# Revit family: TUB
name_source: partatom
category: Mechanical Equipment
units: mm (PartAtom-declared; Revit-internal decimal feet)

## family parameters
Always vertical = Yes
Cut with Voids When Loaded = No
Part Type = Normal
Room Calculation Point = No
Round Connector Dimension = Use Diameter
Shared = No
Work Plane-Based = No

## types (18) — shared parameters
0 = 0' - 0"
1" = 0' - 1"
1' = 1' - 0"
1.5 = 0' - 1 1/2"
2" = 0' - 2"
2' = 2' - 0"
4" = 0' - 4"
D = 0' - 4"
Manufacturer = Loren Cook Company
ONE EIGTH = 0' - 0 1/8"
URL = www.lorencook.com

## per-type parameters (varying)
| type | (A/2)-4" | (A/2)-4.125" | (T_SQ/2)+.125" | -(A/2) | -(C/2) | A | A/2 | A/4 | B | B/2 | C-B | C-B-3" | C_ | C_/2 | E | E+C-B-2" | E-.125" | Model | RO | T_SQ | T_SQ/2 | T_SQ/6 | Type Comments |
| 24_TUB | 0' - 11 5/8" | 0' - 11 1/2" | 1' - 6 1/8" | -1' - 3 5/8" | -0' - 9 9/16" | 2' - 7 1/4" | 1' - 3 5/8" | 0' - 10 13/32" | 1' - 7 1/8" | 0' - 9 9/16" | 2' - 5 1/4" | 2' - 2 1/4" | 4' - 0 3/8" | 2' - 0 3/16" | 0' - 3" | 2' - 6 1/4" | 0' - 2 7/8" | TUB | 2' - 7 1/2" | 3' - 0" | 1' - 6" | 0' - 6" | Upblast Exhaust Ventilator Triton Steel Propeller Roof Mounted/ Belt Drive |
| 30_TUB_SC | 1' - 2 5/8" | 1' - 2 1/2" | 1' - 9 1/8" | -1' - 6 5/8" | -0' - 11 13/16" | 3' - 1 1/4" | 1' - 6 5/8" | 1' - 0 13/32" | 1' - 11 5/8" | 0' - 11 13/16" | 2' - 6 1/2" | 2' - 3 1/2" | 4' - 6 1/8" | 2' - 3 1/16" | 0' - 3" | 2' - 7 1/2" | 0' - 2 7/8" | TUBSC | 3' - 1 1/2" | 3' - 6" | 1' - 9" | 0' - 7" | Upblast Exhaust Smoke Control Ventilator Triton Steel Propeller Roof Mounted/ Belt Drive |
| 36_TUB_SC | 1' - 5 5/8" | 1' - 5 1/2" | 2' - 0 1/8" | -1' - 9 5/8" | -1' - 0 13/16" | 3' - 7 1/4" | 1' - 9 5/8" | 1' - 2 13/32" | 2' - 1 5/8" | 1' - 0 13/16" | 2' - 11 1/2" | 2' - 8 1/2" | 5' - 1 1/8" | 2' - 6 9/16" | 0' - 3" | 3' - 0 1/2" | 0' - 2 7/8" | TUBSC | 3' - 7 1/2" | 4' - 0" | 2' - 0" | 0' - 8" | Upblast Exhaust Smoke Control Ventilator Triton Steel Propeller Roof Mounted/ Belt Drive |
| 42_TUB_SC | 1' - 8 5/8" | 1' - 8 1/2" | 2' - 3 1/8" | -2' - 0 5/8" | -1' - 1 15/16" | 4' - 1 1/4" | 2' - 0 5/8" | 1' - 4 13/32" | 2' - 3 7/8" | 1' - 1 15/16" | 3' - 0 11/16" | 2' - 9 11/16" | 5' - 4 9/16" | 2' - 8 9/32" | 0' - 3" | 3' - 1 11/16" | 0' - 2 7/8" | TUBSC | 4' - 1 1/2" | 4' - 6" | 2' - 3" | 0' - 9" | Upblast Exhaust Smoke Control Ventilator Triton Steel Propeller Roof Mounted/ Belt Drive |
| 48_TUB | 1' - 11 5/8" | 1' - 11 1/2" | 2' - 6 1/8" | -2' - 3 5/8" | -1' - 3 5/8" | 4' - 7 1/4" | 2' - 3 5/8" | 1' - 6 13/32" | 2' - 7 1/4" | 1' - 3 5/8" | 3' - 3 9/16" | 3' - 0 9/16" | 5' - 10 13/16" | 2' - 11 13/32" | 0' - 3" | 3' - 4 9/16" | 0' - 2 7/8" | TUB | 4' - 7 1/2" | 5' - 0" | 2' - 6" | 0' - 10" | Upblast Exhaust Ventilator Triton Steel Propeller Roof Mounted/ Belt Drive |
| 54_TUB | 2' - 2 5/8" | 2' - 2 1/2" | 2' - 9 1/8" | -2' - 6 5/8" | -1' - 5 5/8" | 5' - 1 1/4" | 2' - 6 5/8" | 1' - 8 13/32" | 2' - 11 1/4" | 1' - 5 5/8" | 3' - 8" | 3' - 5" | 6' - 7 1/4" | 3' - 3 5/8" | 0' - 3" | 3' - 9" | 0' - 2 7/8" | TUB | 5' - 1 1/2" | 5' - 6" | 2' - 9" | 0' - 11" | Upblast Exhaust Ventilator Triton Steel Propeller Roof Mounted/ Belt Drive |
| 60_TUB | 2' - 5 5/8" | 2' - 5 1/2" | 3' - 0 1/8" | -2' - 9 5/8" | -1' - 6 1/4" | 5' - 7 1/4" | 2' - 9 5/8" | 1' - 10 13/32" | 3' - 0 1/2" | 1' - 6 1/4" | 3' - 11 1/4" | 3' - 8 1/4" | 6' - 11 3/4" | 3' - 5 7/8" | 0' - 3" | 4' - 0 1/4" | 0' - 2 7/8" | TUB | 5' - 7 1/2" | 6' - 0" | 3' - 0" | 1' - 0" | Upblast Exhaust Ventilator Triton Steel Propeller Roof Mounted/ Belt Drive |
| 72_TUB | 2' - 11 1/2" | 2' - 11 3/8" | 3' - 6 1/8" | -3' - 3 1/2" | -1' - 10" | 6' - 7" | 3' - 3 1/2" | 2' - 2 11/32" | 3' - 8" | 1' - 10" | 4' - 6 13/16" | 4' - 3 13/16" | 8' - 2 13/16" | 4' - 1 13/32" | 0' - 3" | 4' - 7 13/16" | 0' - 2 7/8" | TUB | 6' - 7 1/2" | 7' - 0" | 3' - 6" | 1' - 2" | Upblast Exhaust Ventilator Triton Steel Propeller Roof Mounted/ Belt Drive |
| 20_TUB | 0' - 9 5/8" | 0' - 9 1/2" | 1' - 4 1/8" | -1' - 1 5/8" | -0' - 9 1/16" | 2' - 3 1/4" | 1' - 1 5/8" | 0' - 9 3/32" | 1' - 6 1/8" | 0' - 9 1/16" | 2' - 5 5/8" | 2' - 2 5/8" | 3' - 11 3/4" | 1' - 11 7/8" | 0' - 2" | 2' - 5 5/8" | 0' - 1 7/8" | TUB | 2' - 3 1/2" | 2' - 8" | 1' - 4" | 0' - 5 11/32" | Upblast Exhaust Ventilator Triton Steel Propeller Roof Mounted/ Belt Drive |
| 20_TUB_SC | 0' - 9 5/8" | 0' - 9 1/2" | 1' - 4 1/8" | -1' - 1 5/8" | -0' - 9 1/16" | 2' - 3 1/4" | 1' - 1 5/8" | 0' - 9 3/32" | 1' - 6 1/8" | 0' - 9 1/16" | 2' - 5 5/8" | 2' - 2 5/8" | 3' - 11 3/4" | 1' - 11 7/8" | 0' - 2" | 2' - 5 5/8" | 0' - 1 7/8" | TUBSC | 2' - 3 1/2" | 2' - 8" | 1' - 4" | 0' - 5 11/32" | Upblast Exhaust Smoke Control Ventilator Triton Steel Propeller Roof Mounted/ Belt Drive |
| 24_TUB_SC | 0' - 11 5/8" | 0' - 11 1/2" | 1' - 6 1/8" | -1' - 3 5/8" | -0' - 9 9/16" | 2' - 7 1/4" | 1' - 3 5/8" | 0' - 10 13/32" | 1' - 7 1/8" | 0' - 9 9/16" | 2' - 5 1/4" | 2' - 2 1/4" | 4' - 0 3/8" | 2' - 0 3/16" | 0' - 3" | 2' - 6 1/4" | 0' - 2 7/8" | TUBSC | 2' - 7 1/2" | 3' - 0" | 1' - 6" | 0' - 6" | Upblast Exhaust Smoke Control Ventilator Triton Steel Propeller Roof Mounted/ Belt Drive |
| 48_TUB_SC | 1' - 11 5/8" | 1' - 11 1/2" | 2' - 6 1/8" | -2' - 3 5/8" | -1' - 3 5/8" | 4' - 7 1/4" | 2' - 3 5/8" | 1' - 6 13/32" | 2' - 7 1/4" | 1' - 3 5/8" | 3' - 3 9/16" | 3' - 0 9/16" | 5' - 10 13/16" | 2' - 11 13/32" | 0' - 3" | 3' - 4 9/16" | 0' - 2 7/8" | TUBSC | 4' - 7 1/2" | 5' - 0" | 2' - 6" | 0' - 10" | Upblast Exhaust Smoke Control Ventilator Triton Steel Propeller Roof Mounted/ Belt Drive |
| 30_TUB | 1' - 2 5/8" | 1' - 2 1/2" | 1' - 9 1/8" | -1' - 6 5/8" | -0' - 11 13/16" | 3' - 1 1/4" | 1' - 6 5/8" | 1' - 0 13/32" | 1' - 11 5/8" | 0' - 11 13/16" | 2' - 6 1/2" | 2' - 3 1/2" | 4' - 6 1/8" | 2' - 3 1/16" | 0' - 3" | 2' - 7 1/2" | 0' - 2 7/8" | TUB | 3' - 1 1/2" | 3' - 6" | 1' - 9" | 0' - 7" | Upblast Exhaust Ventilator Triton Steel Propeller Roof Mounted/ Belt Drive |
| 36_TUB | 1' - 5 5/8" | 1' - 5 1/2" | 2' - 0 1/8" | -1' - 9 5/8" | -1' - 0 13/16" | 3' - 7 1/4" | 1' - 9 5/8" | 1' - 2 13/32" | 2' - 1 5/8" | 1' - 0 13/16" | 2' - 11 1/2" | 2' - 8 1/2" | 5' - 1 1/8" | 2' - 6 9/16" | 0' - 3" | 3' - 0 1/2" | 0' - 2 7/8" | TUB | 3' - 7 1/2" | 4' - 0" | 2' - 0" | 0' - 8" | Upblast Exhaust Ventilator Triton Steel Propeller Roof Mounted/ Belt Drive |
| 42_TUB | 1' - 8 5/8" | 1' - 8 1/2" | 2' - 3 1/8" | -2' - 0 5/8" | -1' - 1 15/16" | 4' - 1 1/4" | 2' - 0 5/8" | 1' - 4 13/32" | 2' - 3 7/8" | 1' - 1 15/16" | 3' - 0 11/16" | 2' - 9 11/16" | 5' - 4 9/16" | 2' - 8 9/32" | 0' - 3" | 3' - 1 11/16" | 0' - 2 7/8" | TUB | 4' - 1 1/2" | 4' - 6" | 2' - 3" | 0' - 9" | Upblast Exhaust Ventilator Triton Steel Propeller Roof Mounted/ Belt Drive |
| 54_TUB_SC | 2' - 2 5/8" | 2' - 2 1/2" | 2' - 9 1/8" | -2' - 6 5/8" | -1' - 5 5/8" | 5' - 1 1/4" | 2' - 6 5/8" | 1' - 8 13/32" | 2' - 11 1/4" | 1' - 5 5/8" | 3' - 8" | 3' - 5" | 6' - 7 1/4" | 3' - 3 5/8" | 0' - 3" | 3' - 9" | 0' - 2 7/8" | TUBSC | 5' - 1 1/2" | 5' - 6" | 2' - 9" | 0' - 11" | Upblast Exhaust Smoke Control Ventilator Triton Steel Propeller Roof Mounted/ Belt Drive |
| 60_TUB_SC | 2' - 5 5/8" | 2' - 5 1/2" | 3' - 0 1/8" | -2' - 9 5/8" | -1' - 6 1/4" | 5' - 7 1/4" | 2' - 9 5/8" | 1' - 10 13/32" | 3' - 0 1/2" | 1' - 6 1/4" | 3' - 11 1/4" | 3' - 8 1/4" | 6' - 11 3/4" | 3' - 5 7/8" | 0' - 3" | 4' - 0 1/4" | 0' - 2 7/8" | TUBSC | 5' - 7 1/2" | 6' - 0" | 3' - 0" | 1' - 0" | Upblast Exhaust Smoke Control Ventilator Triton Steel Propeller Roof Mounted/ Belt Drive |
| 72_TUB_SC | 2' - 11 1/2" | 2' - 11 3/8" | 3' - 6 1/8" | -3' - 3 1/2" | -1' - 10" | 6' - 7" | 3' - 3 1/2" | 2' - 2 11/32" | 3' - 8" | 1' - 10" | 4' - 6 13/16" | 4' - 3 13/16" | 8' - 2 13/16" | 4' - 1 13/32" | 0' - 3" | 4' - 7 13/16" | 0' - 2 7/8" | TUBSC | 6' - 7 1/2" | 7' - 0" | 3' - 6" | 1' - 2" | Upblast Exhaust Smoke Control Ventilator Triton Steel Propeller Roof Mounted/ Belt Drive |

## geometry (parser evidence)
native form markers: Sweep x1
no freeform markers — native parametric forms only
